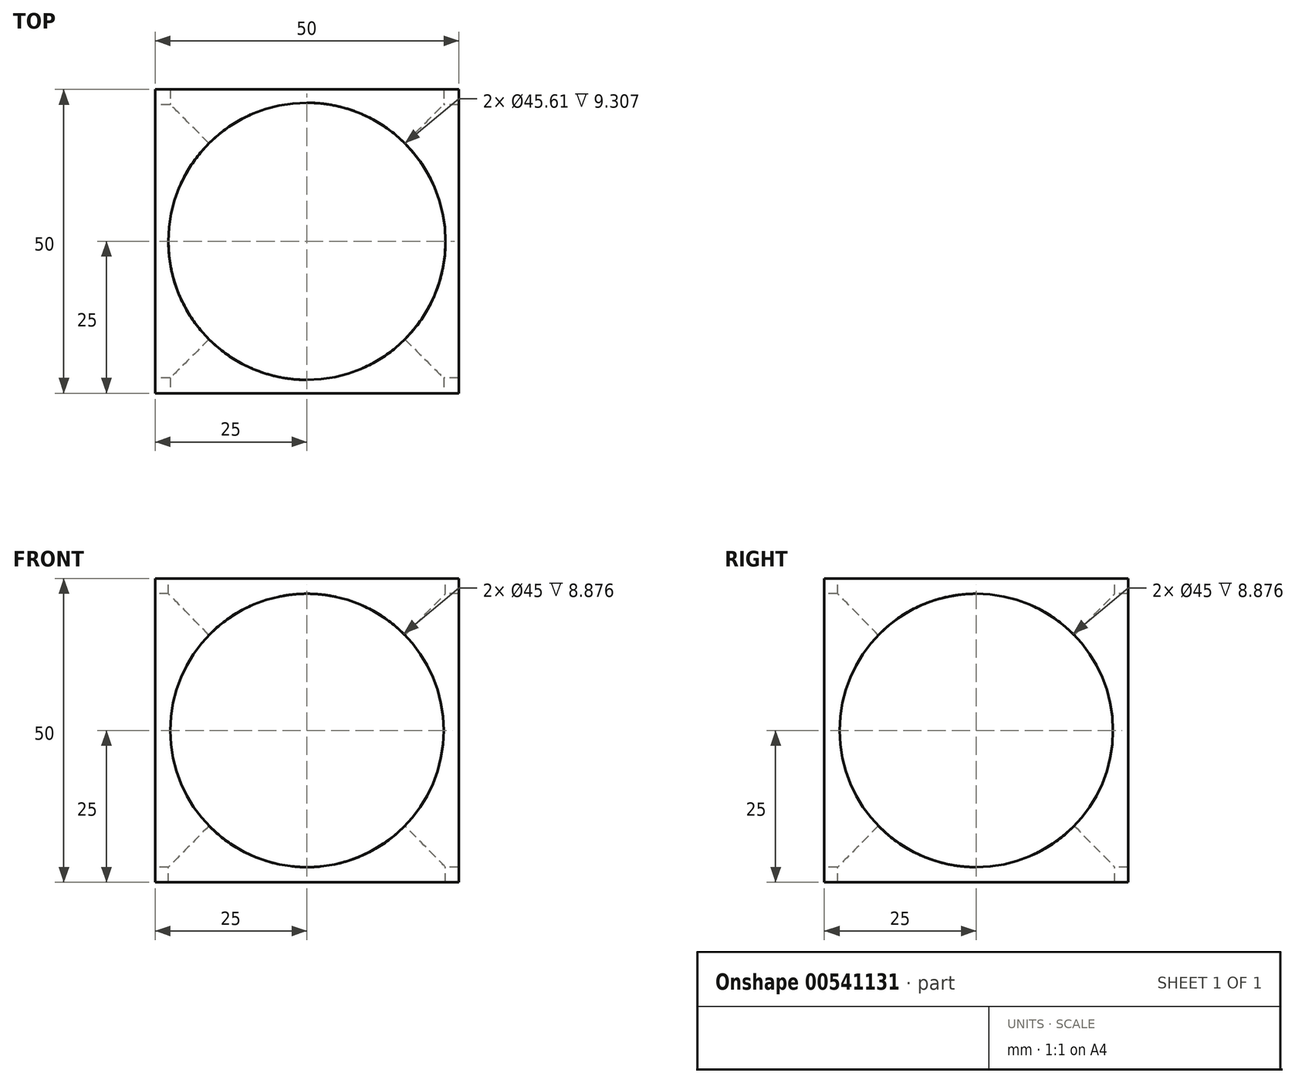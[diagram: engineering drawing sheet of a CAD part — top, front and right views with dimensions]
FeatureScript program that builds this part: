
annotation { "Feature Type Name" : "Feature", "Feature Type Description" : "" }
export const myFeature = defineFeature(function(context is Context, id is Id, definition is map)
    precondition{}
    {
        {
            var Q0;
            Q0=qCreatedBy(makeId("Top.planeOp"),FACE);
            var sketch = newSketch(context, id + "F0", { "sketchPlane" : qUnion([Q0])});
            skLineSegment(sketch, "E0.bottom", {"start": v(25, -25) * mm, "end": v(-25, -25) * mm});
            skLineSegment(sketch, "E0.top", {"start": v(25, 25) * mm, "end": v(-25, 25) * mm});
            skLineSegment(sketch, "E0.left", {"start": v(25, -25) * mm, "end": v(25, 25) * mm});
            skLineSegment(sketch, "E0.right", {"start": v(-25, -25) * mm, "end": v(-25, 25) * mm});
            skPoint(sketch, "E0.middle", {"position": v(0, 0) * mm});
            skSolve(sketch);
        }
        {
            var Q0;
            Q0 = qSketchRegion(id + "F0", true);
            extrude(context, id + "F1", {"entities" : qUnion([Q0]), "flatOperationType" : FlatOperationType.REMOVE, "depth" : 50 * mm, "offsetDistance" : 25 * mm, "domain" : OperationDomain.MODEL});
        }
        {
            var Q0;
            Q0=makeQuery(id+"F1.opExtrude","CAP_FACE",FACE,{"disambiguationData":[OSD([sQuery(id+"F0.wireOp",EDGE,"E0.bottom"),sQuery(id+"F0.wireOp",EDGE,"E0.top"),sQuery(id+"F0.wireOp",EDGE,"E0.left"),sQuery(id+"F0.wireOp",EDGE,"E0.right")])],"isStart":false});
            var sketch = newSketch(context, id + "F2", { "sketchPlane" : qUnion([Q0])});
            skCircle(sketch, "E1", {"center": v(0, 0) * mm, "radius": 22.8 * mm});
            skSolve(sketch);
        }
        {
            var Q0;
            Q0 = qSketchRegion(id + "F2", true);
            extrude(context, id + "F3", {"entities" : qUnion([Q0]), "operationType" : NewBodyOperationType.REMOVE, "oppositeDirection" : true, "depth" : 50 * mm, "offsetDistance" : 25 * mm});
        }
        {
            var Q0;
            Q0=makeQuery(id+"F1.opExtrude","SWEPT_FACE",FACE,{"disambiguationData":[OSD([sQuery(id+"F0.wireOp",EDGE,"E0.bottom")])]});
            var sketch = newSketch(context, id + "F4", { "sketchPlane" : qUnion([Q0])});
            skCircle(sketch, "E2", {"center": v(0, 25) * mm, "radius": 22.5 * mm});
            skSolve(sketch);
        }
        {
            var Q0;
            Q0=makeQuery(id+"F4.imprint","IMPRINT",FACE,{"disambiguationData":[TD([[makeQuery(id+"F4.imprint","IMPRINT",EDGE,{"derivedFrom":sQuery(id+"F4.wireOp",EDGE,"E2")}),1.0]])]});
            extrude(context, id + "F5", {"entities" : qUnion([Q0]), "operationType" : NewBodyOperationType.REMOVE, "oppositeDirection" : true, "depth" : 50 * mm, "offsetDistance" : 25 * mm});
        }
        {
            var Q0;
            Q0=makeQuery(id+"F1.opExtrude","SWEPT_FACE",FACE,{"disambiguationData":[OSD([sQuery(id+"F0.wireOp",EDGE,"E0.right")])]});
            var sketch = newSketch(context, id + "F6", { "sketchPlane" : qUnion([Q0])});
            skCircle(sketch, "E3", {"center": v(0, 25) * mm, "radius": 22.5 * mm});
            skSolve(sketch);
        }
        {
            var Q0;
            Q0=makeQuery(id+"F6.imprint","IMPRINT",FACE,{"disambiguationData":[TD([[makeQuery(id+"F6.imprint","IMPRINT",EDGE,{"derivedFrom":sQuery(id+"F6.wireOp",EDGE,"E3")}),1.0]])]});
            extrude(context, id + "F7", {"entities" : qUnion([Q0]), "operationType" : NewBodyOperationType.REMOVE, "oppositeDirection" : true, "depth" : 50 * mm, "offsetDistance" : 25 * mm});
        }
    });
